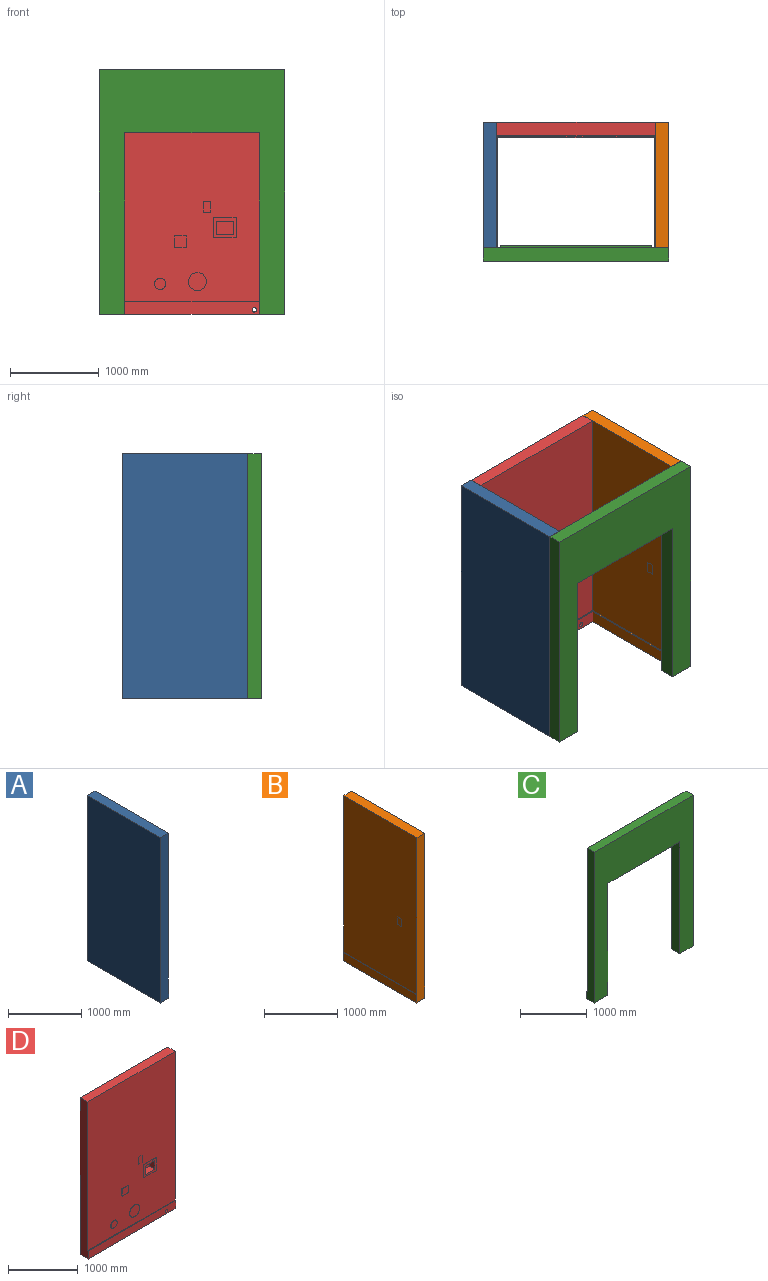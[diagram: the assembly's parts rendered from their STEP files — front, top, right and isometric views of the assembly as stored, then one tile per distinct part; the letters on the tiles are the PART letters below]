
ASSEMBLY  parts=4 mates=9
PART A: 8 faces, bbox 165.1x1409.7x2755.9 mm
  f0: plane 1409.7x165.1mm, normal (0,0,-1), area 232741.5mm2, adj f2,f3,f6,f7
  f1: plane 1409.7x152.4mm, normal (0,0,1), area 214838.3mm2, adj f2,f3,f4,f7
  f2: plane 2755.9x165.1mm, normal (0,-1,0), area 421773.4mm2, adj f0,f1,f3,f4,f5,f6
  f3: plane 2755.9x1409.7mm, normal (-1,0,0), area 3884992.2mm2, adj f0,f1,f2,f7
  f4: plane 2616.2x1409.7mm, normal (1,0,0), area 3688057.1mm2, adj f1,f2,f5,f7
  f5: plane 1409.7x12.7mm, normal (0,0,1), area 17903.2mm2, adj f2,f4,f6,f7
  f6: plane 1409.7x139.7mm, normal (1,0,0), area 196935.1mm2, adj f0,f2,f5,f7
  f7: plane 2755.9x165.1mm, normal (0,1,0), area 421773.4mm2, adj f0,f1,f3,f4,f5,f6
PART B: 13 faces, bbox 165.1x1409.7x2755.9 mm
  f0: plane 2616.2x1409.7mm, normal (-1,0,0), area 3678228.5mm2, adj f1,f3,f5,f6,f7,f8,f10,f12
  f1: plane 2755.9x165.1mm, normal (0,-1,0), area 421773.3mm2, adj f0,f2,f3,f4,f10,f11
  f2: plane 1409.7x165.1mm, normal (0,0,-1), area 232741.5mm2, adj f1,f4,f11,f12
  f3: plane 1409.7x152.4mm, normal (0,0,1), area 214838.3mm2, adj f0,f1,f4,f12
  f4: plane 2755.9x1409.7mm, normal (1,0,0), area 3884992.2mm2, adj f1,f2,f3,f12
  f5: plane 79.38x6.35mm, normal (0,0,1), area 504mm2, adj f0,f6,f8,f9
  f6: plane 123.83x6.35mm, normal (0,-1,0), area 786.3mm2, adj f0,f5,f7,f9
  f7: plane 79.38x6.35mm, normal (0,0,-1), area 504mm2, adj f0,f6,f8,f9
  f8: plane 123.83x6.35mm, normal (0,1,0), area 786.3mm2, adj f0,f5,f7,f9
  f9: plane 123.83x79.38mm, normal (-1,0,0), area 9828.6mm2, adj f5,f6,f7,f8
  f10: plane 1409.7x12.7mm, normal (0,0,1), area 17903.2mm2, adj f0,f1,f11,f12
  f11: plane 1409.7x139.7mm, normal (-1,0,0), area 196935.1mm2, adj f1,f2,f10,f12
  f12: plane 2755.9x165.1mm, normal (0,1,0), area 421773.3mm2, adj f0,f2,f3,f4,f10,f11
PART C: 18 faces, bbox 2089.2x177.8x2755.9 mm
  f0: plane 2616.2x2089.15mm, normal (0,1,0), area 2038060.4mm2, adj f6,f8,f9,f10,f12,f14,f16,f17
  f1: plane 288.93x177.8mm, normal (0,0,-1), area 47741.8mm2, adj f2,f7,f10,f11,f15,f17
  f2: plane 2044.7x177.8mm, normal (1,0,0), area 363547.7mm2, adj f1,f3,f7,f11
  f3: plane 1511.3x177.8mm, normal (0,0,-1), area 268709.1mm2, adj f2,f4,f7,f11
  f4: plane 2044.7x177.8mm, normal (-1,0,0), area 363547.7mm2, adj f3,f5,f7,f11
  f5: plane 288.93x177.8mm, normal (0,0,-1), area 47741.8mm2, adj f4,f7,f8,f11,f13,f16
  f6: plane 2089.15x152.4mm, normal (0,0,1), area 318386.5mm2, adj f0,f7,f16,f17
  f7: plane 2755.9x2089.15mm, normal (0,-1,0), area 2667333.4mm2, adj f1,f2,f3,f4,f5,f6,f16,f17
  f8: plane 2146.3x25.4mm, normal (1,0,0), area 53628.9mm2, adj f0,f5,f9,f11,f12,f13
  f9: plane 1708.15x25.4mm, normal (0,0,1), area 43387mm2, adj f0,f8,f10,f11
  f10: plane 2146.3x25.4mm, normal (-1,0,0), area 53628.9mm2, adj f0,f1,f9,f11,f14,f15
  f11: plane 2146.3x1708.15mm, normal (0,1,0), area 576047.2mm2, adj f1,f2,f3,f4,f5,f8,f9,f10
  f12: plane 190.5x6.35mm, normal (0,0,1), area 1209.7mm2, adj f0,f8,f13,f16
  f13: plane 190.5x139.7mm, normal (0,1,0), area 26612.8mm2, adj f5,f8,f12,f16
  f14: plane 190.5x6.35mm, normal (0,0,1), area 1209.7mm2, adj f0,f10,f15,f17
  f15: plane 190.5x139.7mm, normal (0,1,0), area 26612.8mm2, adj f1,f10,f14,f17
  f16: plane 2755.9x158.75mm, normal (1,0,0), area 420886.3mm2, adj f0,f5,f6,f7,f12,f13
  f17: plane 2755.9x158.75mm, normal (-1,0,0), area 420886.3mm2, adj f0,f1,f6,f7,f14,f15
PART D: 33 faces, bbox 1784.4x165.1x2755.9 mm
  f0: plane 2616.2x1784.35mm, normal (0,-1,0), area 4539546.1mm2, adj f1,f3,f5,f7,f8,f9,f14,f16
  f1: plane 2755.9x165.1mm, normal (-1,0,0), area 421773.3mm2, adj f0,f2,f5,f6,f31,f32
  f2: plane 1784.35x165.1mm, normal (0,0,-1), area 294596.2mm2, adj f1,f3,f6,f32
  f3: plane 2755.9x165.1mm, normal (1,0,0), area 421773.3mm2, adj f0,f2,f5,f6,f31,f32
  f4: cylinder r=25.4mm len=165.1mm, axis (0,-1,0), area 26348.8mm2, adj f6,f32
  f5: plane 1784.35x152.4mm, normal (0,0,1), area 271934.9mm2, adj f0,f1,f3,f6
  f6: plane 2755.9x1784.35mm, normal (0,1,0), area 4915463.3mm2, adj f1,f2,f3,f4,f5
  f7: plane 255.59x6.35mm, normal (0,0,1), area 1623mm2, adj f0,f8,f14,f15
  f8: plane 225.43x6.35mm, normal (-1,0,0), area 1431.4mm2, adj f0,f7,f9,f15
  f9: plane 255.59x6.35mm, normal (0,0,-1), area 1623mm2, adj f0,f8,f14,f15
  f10: plane 149.23x107.95mm, normal (-1,0,0), area 16108.8mm2, adj f11,f13,f15,f30
  f11: plane 192.09x107.95mm, normal (0,0,1), area 20735.8mm2, adj f10,f12,f15,f30
  f12: plane 149.23x107.95mm, normal (1,0,0), area 16108.8mm2, adj f11,f13,f15,f30
  f13: plane 192.09x107.95mm, normal (0,0,-1), area 20735.8mm2, adj f10,f12,f15,f30
  f14: plane 225.43x6.35mm, normal (1,0,0), area 1431.4mm2, adj f0,f7,f9,f15
  f15: plane 255.59x225.43mm, normal (0,-1,0), area 28951.6mm2, adj f7,f8,f9,f10,f11,f12,f13,f14
  f16: cylinder r=63.5mm len=127mm, axis (0,1,0), area 2533.5mm2, adj f0,f17
  f17: plane 127x127mm, normal (0,-1,0), area 12667.7mm2, adj f16
  f18: plane 127x6.35mm, normal (0,0,1), area 806.5mm2, adj f0,f19,f21,f22
  f19: plane 127x6.35mm, normal (-1,0,0), area 806.5mm2, adj f0,f18,f20,f22
  f20: plane 127x6.35mm, normal (0,0,-1), area 806.5mm2, adj f0,f19,f21,f22
  f21: plane 127x6.35mm, normal (1,0,0), area 806.5mm2, adj f0,f18,f20,f22
  f22: plane 127x127mm, normal (0,-1,0), area 16129mm2, adj f18,f19,f20,f21
  f23: plane 79.38x6.35mm, normal (0,0,1), area 504mm2, adj f0,f24,f26,f27
  f24: plane 123.83x6.35mm, normal (-1,0,0), area 786.3mm2, adj f0,f23,f25,f27
  f25: plane 79.38x6.35mm, normal (0,0,-1), area 504mm2, adj f0,f24,f26,f27
  f26: plane 123.83x6.35mm, normal (1,0,0), area 786.3mm2, adj f0,f23,f25,f27
  f27: plane 123.83x79.38mm, normal (0,-1,0), area 9828.6mm2, adj f23,f24,f25,f26
  f28: cylinder r=101.6mm len=203.2mm, axis (0,1,0), area 4053.7mm2, adj f0,f29
  f29: plane 203.2x203.2mm, normal (0,-1,0), area 32429.3mm2, adj f28
  f30: plane 192.09x149.23mm, normal (0,-1,0), area 28664.3mm2, adj f10,f11,f12,f13
  f31: plane 1784.35x12.7mm, normal (0,0,1), area 22661.2mm2, adj f0,f1,f3,f32
  f32: plane 1784.35x139.7mm, normal (0,-1,0), area 247246.9mm2, adj f1,f2,f3,f4,f31
PLACE A t=(152.4,1409.7,0)mm
PLACE B t=(152.4,1409.7,0)mm
PLACE C t=(152.4,1409.7,0)mm
PLACE D t=(152.4,1409.7,0)mm
MATE planar D.f6 <-> B.f12  axis (0,1,0) through (1044.29,1562.1,1378.5)mm
MATE planar D.f2 <-> B.f2  axis (0,0,-1) through (1044.58,1479.55,0)mm
MATE planar C.f1 <-> A.f0  axis (0,0,-1) through (148.2,82.87,0)mm
MATE planar C.f16 <-> B.f4  axis (1,0,0) through (2089.15,76.37,1375.19)mm
MATE planar A.f0 <-> B.f2  axis (0,0,-1) through (82.55,857.25,0)mm
MATE planar B.f1 <-> C.f0  axis (0,-1,0) through (2012.6,152.4,1372.45)mm
MATE planar D.f1 <-> A.f4  axis (-1,0,0) through (152.4,1485.55,1372.45)mm
MATE planar B.f0 <-> D.f3  axis (-1,0,0) through (1936.75,858.24,1448.5)mm
MATE planar A.f2 <-> C.f0  axis (0,-1,0) through (76.55,152.4,1372.45)mm
